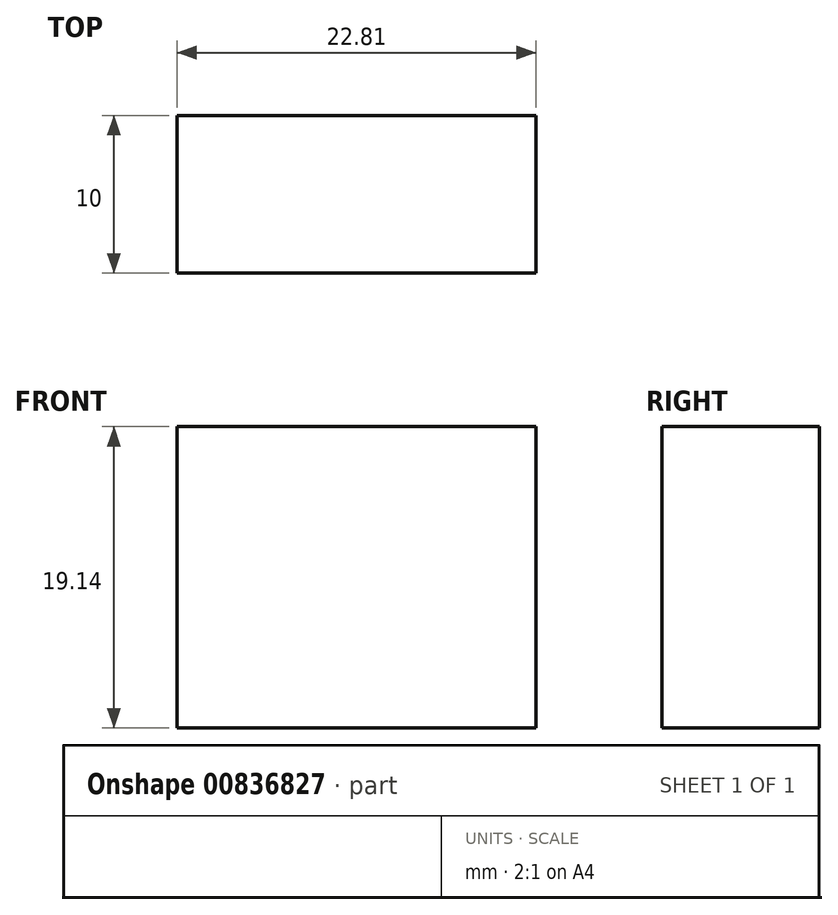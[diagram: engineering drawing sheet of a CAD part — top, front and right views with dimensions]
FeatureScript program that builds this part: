
annotation { "Feature Type Name" : "Feature", "Feature Type Description" : "" }
export const myFeature = defineFeature(function(context is Context, id is Id, definition is map)
    precondition{}
    {
        {
            var Q0;
            Q0=qCreatedBy(makeId("Front.planeOp"),FACE);
            var sketch = newSketch(context, id + "F0", { "sketchPlane" : qUnion([Q0])});
            skLineSegment(sketch, "E0.bottom", {"start": v(-11.64, 11.64) * mm, "end": v(11.17, 11.64) * mm});
            skLineSegment(sketch, "E0.top", {"start": v(-11.64, -7.5) * mm, "end": v(11.17, -7.5) * mm});
            skLineSegment(sketch, "E0.left", {"start": v(-11.64, 11.64) * mm, "end": v(-11.64, -7.5) * mm});
            skLineSegment(sketch, "E0.right", {"start": v(11.17, 11.64) * mm, "end": v(11.17, -7.5) * mm});
            skSolve(sketch);
        }
        {
            var Q0;
            Q0=makeQuery(id+"F0.imprint","IMPRINT",FACE,{"disambiguationData":[TD([[makeQuery(id+"F0.imprint","IMPRINT",EDGE,{"derivedFrom":sQuery(id+"F0.wireOp",EDGE,"E0.bottom")}),-1.0]])]});
            extrude(context, id + "F1", {"entities" : qUnion([Q0]), "depth" : 10 * mm, "offsetDistance" : 25 * mm});
        }
    });
